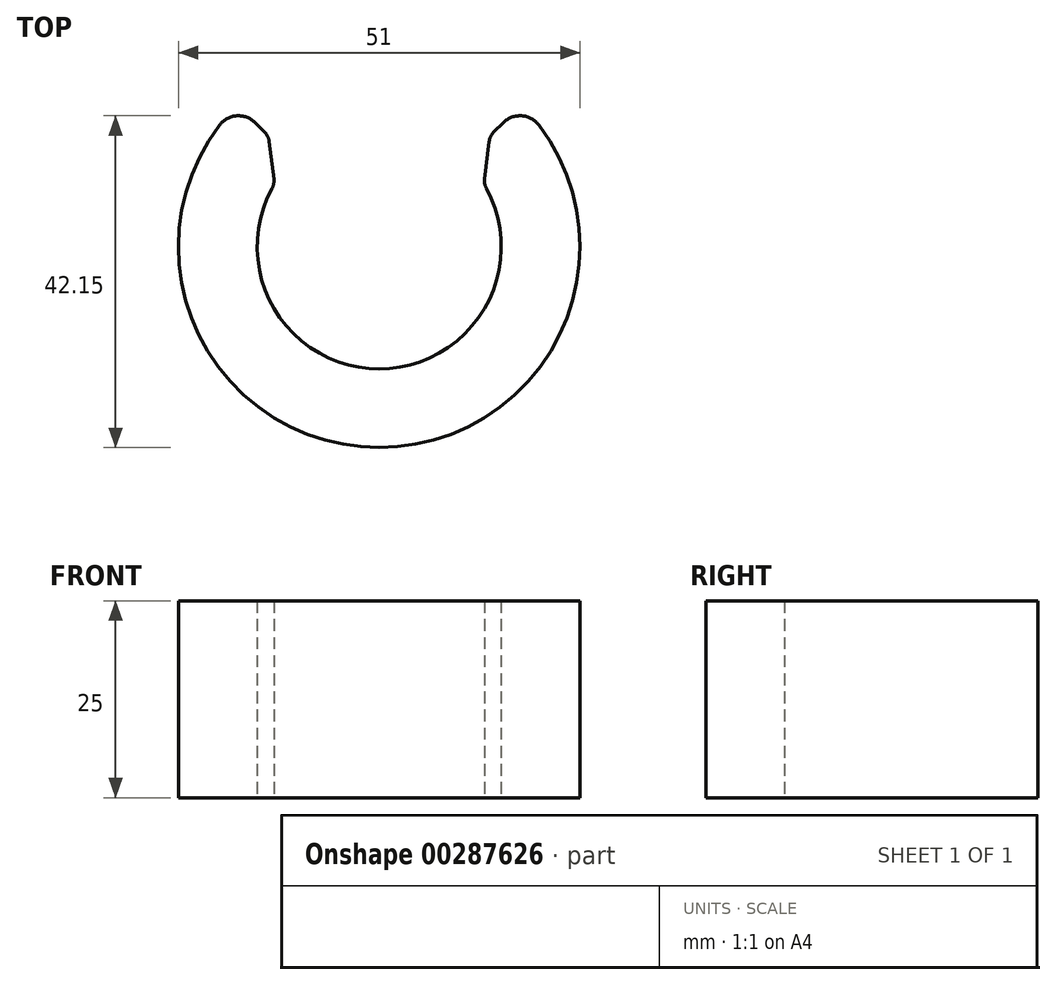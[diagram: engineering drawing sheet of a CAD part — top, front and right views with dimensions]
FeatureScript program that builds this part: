
annotation { "Feature Type Name" : "Feature", "Feature Type Description" : "" }
export const myFeature = defineFeature(function(context is Context, id is Id, definition is map)
    precondition{}
    {
        {
            var Q0;
            Q0=qCreatedBy(makeId("Top.planeOp"),FACE);
            var sketch = newSketch(context, id + "F0", { "sketchPlane" : qUnion([Q0])});
            skCircle(sketch, "E0", {"center": v(0, 0) * mm, "radius": 15.5 * mm});
            skCircle(sketch, "E1", {"center": v(0, 0) * mm, "radius": 30.5 * mm});
            skCircle(sketch, "E2", {"center": v(0, 0) * mm, "radius": 25.5 * mm});
            skLineSegment(sketch, "E3", {"start": v(0, 0) * mm, "end": v(-21.57, 21.57) * mm});
            skLineSegment(sketch, "E4.MirrorCS", {"start": v(0, 0) * mm, "end": v(21.57, 21.57) * mm});
            skSolve(sketch);
        }
        {
            var Q0;
            {var subQ0=sQuery(id+"F0.wireOp",EDGE,"E3");var subQ1=sQuery(id+"F0.wireOp",EDGE,"E0");var subQ2=makeQuery(id+"F0.imprint","INTERSECT",VERTEX,{"derivedFrom":[subQ1,subQ0]});Q0=makeQuery(id+"F0.imprint","IMPRINT",FACE,{"disambiguationData":[TD([[makeQuery(id+"F0.imprint","IMPRINT",EDGE,{"disambiguationData":[TD([[subQ2,-1.0]])],"derivedFrom":subQ1}),-1.0]])]});}
            extrude(context, id + "F1", {"entities" : qUnion([Q0]), "depth" : 25 * mm});
        }
        {
            var Q0;
            Q0=makeQuery(id+"F1.opExtrude","SWEPT_EDGE",EDGE,{"disambiguationData":[OSD([sQuery(id+"F0.wireOp",EDGE,"E2"),sQuery(id+"F0.wireOp",EDGE,"E3")])]});
            var Q1;
            Q1=makeQuery(id+"F1.opExtrude","SWEPT_EDGE",EDGE,{"disambiguationData":[OSD([sQuery(id+"F0.wireOp",EDGE,"E2"),sQuery(id+"F0.wireOp",EDGE,"E4.MirrorCS")])]});
            fillet(context, id + "F2", {"entities" : qUnion([Q0, Q1]), "radius" : 3 * mm, "tangentPropagation" : true, "allowEdgeOverflow" : false});
        }
        {
            var Q0;
            Q0=makeQuery(id+"F1.opExtrude","SWEPT_EDGE",EDGE,{"disambiguationData":[OSD([sQuery(id+"F0.wireOp",EDGE,"E0"),sQuery(id+"F0.wireOp",EDGE,"E3")])]});
            var Q1;
            Q1=makeQuery(id+"F1.opExtrude","SWEPT_EDGE",EDGE,{"disambiguationData":[OSD([sQuery(id+"F0.wireOp",EDGE,"E0"),sQuery(id+"F0.wireOp",EDGE,"E4.MirrorCS")])]});
            chamfer(context, id + "F3", {"entities" : qUnion([Q0, Q1]), "width" : 5 * mm, "tangentPropagation" : true});
        }
        {
            var Q0;
            {var subQ0=sQuery(id+"F0.wireOp",EDGE,"E0");Q0=makeQuery(id+"F3.opChamfer","BLEND_EDGE",EDGE,{"blendedFrom":[makeQuery(id+"F1.opExtrude","SWEPT_EDGE",EDGE,{"disambiguationData":[OSD([subQ0,sQuery(id+"F0.wireOp",EDGE,"E3")])]}),makeQuery(id+"F1.opExtrude","SWEPT_FACE",FACE,{"disambiguationData":[OSD([subQ0])]})],"blendedInto":[makeQuery(id+"F1.opExtrude","SWEPT_FACE",FACE,{"disambiguationData":[OSD([subQ0])]})]});}
            var Q1;
            {var subQ0=sQuery(id+"F0.wireOp",EDGE,"E3");Q1=makeQuery(id+"F3.opChamfer","BLEND_EDGE",EDGE,{"blendedFrom":[makeQuery(id+"F1.opExtrude","SWEPT_EDGE",EDGE,{"disambiguationData":[OSD([sQuery(id+"F0.wireOp",EDGE,"E0"),subQ0])]}),makeQuery(id+"F1.opExtrude","SWEPT_FACE",FACE,{"disambiguationData":[OSD([subQ0])]})],"blendedInto":[makeQuery(id+"F1.opExtrude","SWEPT_FACE",FACE,{"disambiguationData":[OSD([subQ0])]})]});}
            var Q2;
            {var subQ0=sQuery(id+"F0.wireOp",EDGE,"E0");Q2=makeQuery(id+"F3.opChamfer","BLEND_EDGE",EDGE,{"blendedFrom":[makeQuery(id+"F1.opExtrude","SWEPT_EDGE",EDGE,{"disambiguationData":[OSD([subQ0,sQuery(id+"F0.wireOp",EDGE,"E4.MirrorCS")])]}),makeQuery(id+"F1.opExtrude","SWEPT_FACE",FACE,{"disambiguationData":[OSD([subQ0])]})],"blendedInto":[makeQuery(id+"F1.opExtrude","SWEPT_FACE",FACE,{"disambiguationData":[OSD([subQ0])]})]});}
            var Q3;
            {var subQ0=sQuery(id+"F0.wireOp",EDGE,"E4.MirrorCS");Q3=makeQuery(id+"F3.opChamfer","BLEND_EDGE",EDGE,{"blendedFrom":[makeQuery(id+"F1.opExtrude","SWEPT_EDGE",EDGE,{"disambiguationData":[OSD([sQuery(id+"F0.wireOp",EDGE,"E0"),subQ0])]}),makeQuery(id+"F1.opExtrude","SWEPT_FACE",FACE,{"disambiguationData":[OSD([subQ0])]})],"blendedInto":[makeQuery(id+"F1.opExtrude","SWEPT_FACE",FACE,{"disambiguationData":[OSD([subQ0])]})]});}
            fillet(context, id + "F4", {"entities" : qUnion([Q0, Q1, Q2, Q3]), "radius" : 2 * mm, "tangentPropagation" : true, "allowEdgeOverflow" : false});
        }
    });
